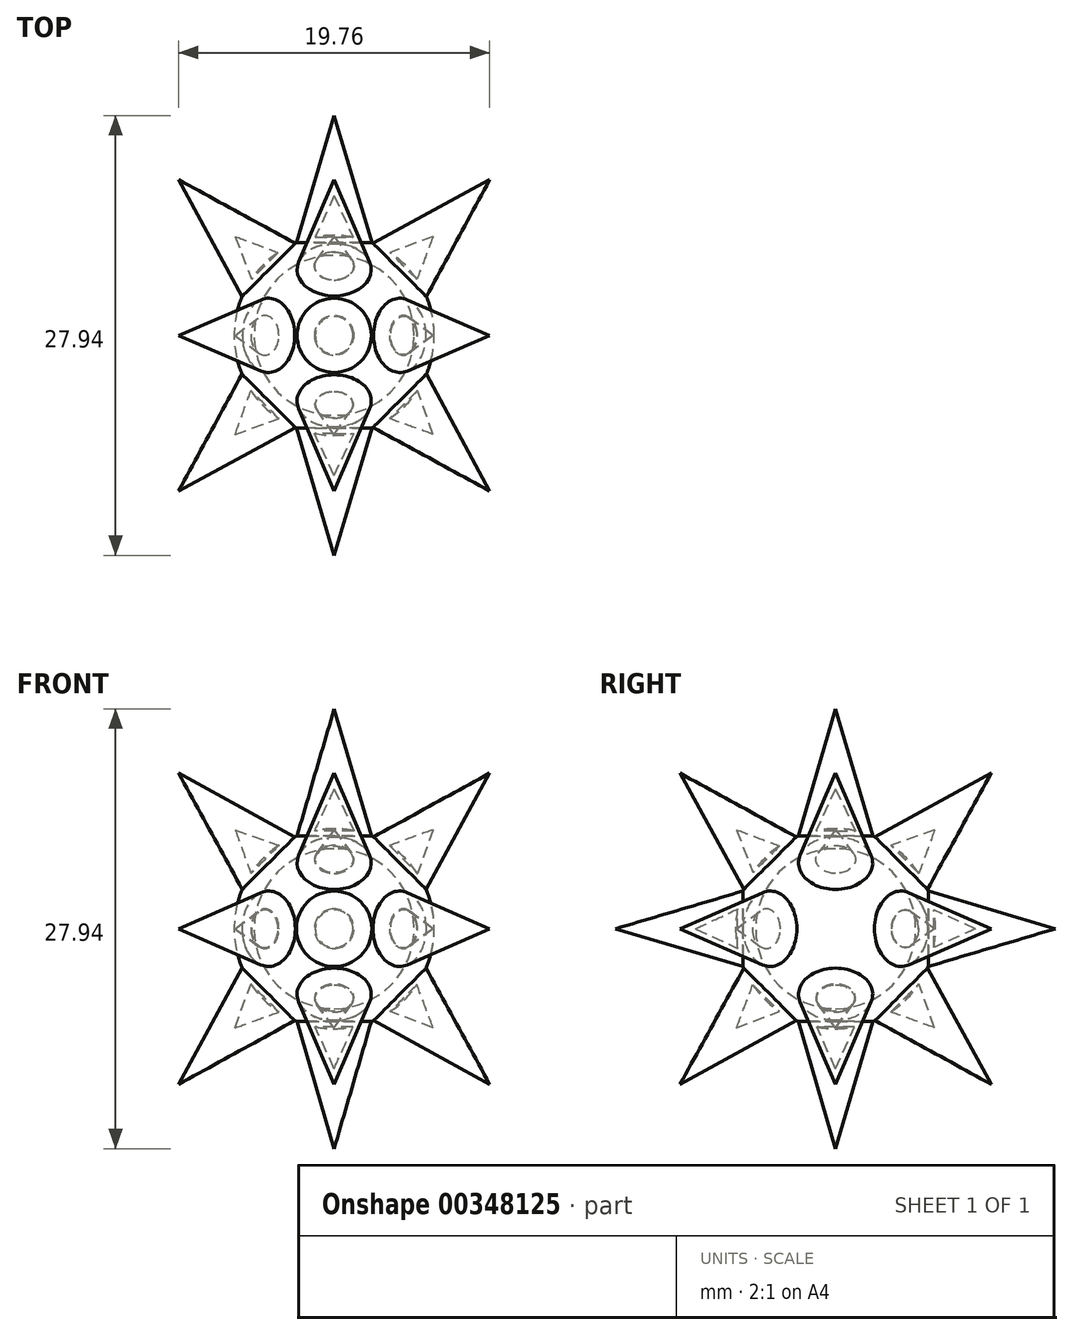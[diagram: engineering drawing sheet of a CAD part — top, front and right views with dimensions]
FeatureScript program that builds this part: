
annotation { "Feature Type Name" : "Feature", "Feature Type Description" : "" }
export const myFeature = defineFeature(function(context is Context, id is Id, definition is map)
    precondition{}
    {
        {
            var Q0;
            Q0=qCreatedBy(makeId("Front.planeOp"),FACE);
            var sketch = newSketch(context, id + "F0", { "sketchPlane" : qUnion([Q0])});
            skCircle(sketch, "E0", {"center": v(0, 0) * mm, "radius": 6.35 * mm});
            skCircle(sketch, "E1", {"center": v(0, 0) * mm, "radius": 5.08 * mm});
            skLineSegment(sketch, "E2", {"start": v(-2.36, 5.9) * mm, "end": v(0, 13.97) * mm});
            skLineSegment(sketch, "E3", {"start": v(0, 13.97) * mm, "end": v(2.36, 5.9) * mm});
            skLineSegment(sketch, "E4", {"start": v(0, 6.89) * mm, "end": v(0, -7.26) * mm, "construction": true});
            skLineSegment(sketch, "E5", {"start": v(0, 13.97) * mm, "end": v(0, -6.35) * mm});
            skLineSegment(sketch, "E6", {"start": v(1.26, 6.22) * mm, "end": v(0, 8.9) * mm});
            skLineSegment(sketch, "E7", {"start": v(0, 8.9) * mm, "end": v(-1.2, 6.24) * mm});
            skLineSegment(sketch, "E8.1.0", {"start": v(-9.88, 9.88) * mm, "end": v(-2.5, 5.84) * mm});
            skLineSegment(sketch, "E8.1.1", {"start": v(-3.51, 5.29) * mm, "end": v(-6.29, 6.29) * mm});
            skLineSegment(sketch, "E8.1.2", {"start": v(-6.29, 6.29) * mm, "end": v(-5.26, 3.56) * mm});
            skLineSegment(sketch, "E8.1.3", {"start": v(-5.84, 2.5) * mm, "end": v(-9.88, 9.88) * mm});
            skLineSegment(sketch, "E8.1.4", {"start": v(-9.88, 9.88) * mm, "end": v(4.5, -4.5) * mm});
            skLineSegment(sketch, "E8.2.0", {"start": v(-13.97, 0) * mm, "end": v(-5.9, 2.36) * mm});
            skLineSegment(sketch, "E8.2.1", {"start": v(-6.22, 1.26) * mm, "end": v(-8.9, 0) * mm});
            skLineSegment(sketch, "E8.2.2", {"start": v(-8.9, 0) * mm, "end": v(-6.24, -1.2) * mm});
            skLineSegment(sketch, "E8.2.3", {"start": v(-5.9, -2.36) * mm, "end": v(-13.97, 0) * mm});
            skLineSegment(sketch, "E8.2.4", {"start": v(-13.97, 0) * mm, "end": v(6.35, 0) * mm});
            skLineSegment(sketch, "E8.3.0", {"start": v(-9.88, -9.88) * mm, "end": v(-5.84, -2.5) * mm});
            skLineSegment(sketch, "E8.3.1", {"start": v(-5.29, -3.51) * mm, "end": v(-6.29, -6.29) * mm});
            skLineSegment(sketch, "E8.3.2", {"start": v(-6.29, -6.29) * mm, "end": v(-3.56, -5.26) * mm});
            skLineSegment(sketch, "E8.3.3", {"start": v(-2.5, -5.84) * mm, "end": v(-9.88, -9.88) * mm});
            skLineSegment(sketch, "E8.3.4", {"start": v(-9.88, -9.88) * mm, "end": v(4.5, 4.5) * mm});
            skLineSegment(sketch, "E8.4.0", {"start": v(0, -13.97) * mm, "end": v(-2.36, -5.9) * mm});
            skLineSegment(sketch, "E8.4.1", {"start": v(-1.26, -6.22) * mm, "end": v(0, -8.9) * mm});
            skLineSegment(sketch, "E8.4.2", {"start": v(0, -8.9) * mm, "end": v(1.2, -6.24) * mm});
            skLineSegment(sketch, "E8.4.3", {"start": v(2.36, -5.9) * mm, "end": v(0, -13.97) * mm});
            skLineSegment(sketch, "E8.4.4", {"start": v(0, -13.97) * mm, "end": v(0, 6.35) * mm});
            skLineSegment(sketch, "E8.5.0", {"start": v(9.88, -9.88) * mm, "end": v(2.5, -5.84) * mm});
            skLineSegment(sketch, "E8.5.1", {"start": v(3.51, -5.29) * mm, "end": v(6.29, -6.29) * mm});
            skLineSegment(sketch, "E8.5.2", {"start": v(6.29, -6.29) * mm, "end": v(5.26, -3.56) * mm});
            skLineSegment(sketch, "E8.5.3", {"start": v(5.84, -2.5) * mm, "end": v(9.88, -9.88) * mm});
            skLineSegment(sketch, "E8.5.4", {"start": v(9.88, -9.88) * mm, "end": v(-4.5, 4.5) * mm});
            skLineSegment(sketch, "E8.6.0", {"start": v(13.97, 0) * mm, "end": v(5.9, -2.36) * mm});
            skLineSegment(sketch, "E8.6.1", {"start": v(6.22, -1.26) * mm, "end": v(8.9, 0) * mm});
            skLineSegment(sketch, "E8.6.2", {"start": v(8.9, 0) * mm, "end": v(6.24, 1.2) * mm});
            skLineSegment(sketch, "E8.6.3", {"start": v(5.9, 2.36) * mm, "end": v(13.97, 0) * mm});
            skLineSegment(sketch, "E8.6.4", {"start": v(13.97, 0) * mm, "end": v(-6.35, 0) * mm});
            skLineSegment(sketch, "E8.7.0", {"start": v(9.88, 9.88) * mm, "end": v(5.84, 2.5) * mm});
            skLineSegment(sketch, "E8.7.1", {"start": v(5.29, 3.51) * mm, "end": v(6.29, 6.29) * mm});
            skLineSegment(sketch, "E8.7.2", {"start": v(6.29, 6.29) * mm, "end": v(3.56, 5.26) * mm});
            skLineSegment(sketch, "E8.7.3", {"start": v(2.5, 5.84) * mm, "end": v(9.88, 9.88) * mm});
            skLineSegment(sketch, "E8.7.4", {"start": v(9.88, 9.88) * mm, "end": v(-4.5, -4.5) * mm});
            skSolve(sketch);
        }
        {
            var Q0;
            {var subQ1=sQuery(id+"F0.wireOp",EDGE,"E0");var subQ5=makeQuery(id+"F0.imprint","INTERSECT",VERTEX,{"derivedFrom":[subQ1,sQuery(id+"F0.wireOp",EDGE,"E3")]});Q0=makeQuery(id+"F0.imprint","IMPRINT",FACE,{"disambiguationData":[TD([[makeQuery(id+"F0.imprint","IMPRINT",EDGE,{"disambiguationData":[TD([[subQ5,-1.0]])],"derivedFrom":subQ1}),1.0]])]});}
            var Q1;
            {var subQ0=sQuery(id+"F0.wireOp",EDGE,"E0");var subQ4=makeQuery(id+"F0.imprint","INTERSECT",VERTEX,{"derivedFrom":[subQ0,sQuery(id+"F0.wireOp",EDGE,"E8.6.2")]});Q1=makeQuery(id+"F0.imprint","IMPRINT",FACE,{"disambiguationData":[TD([[makeQuery(id+"F0.imprint","IMPRINT",EDGE,{"disambiguationData":[TD([[subQ4,1.0]])],"derivedFrom":subQ0}),1.0]])]});}
            var Q2;
            {var subQ0=sQuery(id+"F0.wireOp",EDGE,"E0");var subQ4=makeQuery(id+"F0.imprint","INTERSECT",VERTEX,{"derivedFrom":[subQ0,sQuery(id+"F0.wireOp",EDGE,"E8.5.2")]});Q2=makeQuery(id+"F0.imprint","IMPRINT",FACE,{"disambiguationData":[TD([[makeQuery(id+"F0.imprint","IMPRINT",EDGE,{"disambiguationData":[TD([[subQ4,1.0]])],"derivedFrom":subQ0}),1.0]])]});}
            var Q3;
            {var subQ0=sQuery(id+"F0.wireOp",EDGE,"E0");var subQ8=makeQuery(id+"F0.imprint","INTERSECT",VERTEX,{"derivedFrom":[subQ0,sQuery(id+"F0.wireOp",EDGE,"E8.4.2")]});Q3=makeQuery(id+"F0.imprint","IMPRINT",FACE,{"disambiguationData":[TD([[makeQuery(id+"F0.imprint","IMPRINT",EDGE,{"disambiguationData":[TD([[subQ8,1.0]])],"derivedFrom":subQ0}),1.0]])]});}
            var Q4;
            Q4=sQuery(id+"F0.wireOp",EDGE,"E4");
            revolve(context, id + "F1", {"entities" : qUnion([Q0, Q1, Q2, Q3]), "axis" : qUnion([Q4]), "revolveType" : RevolveType.FULL});
        }
        {
            var Q0;
            {var subQ0=sQuery(id+"F0.wireOp",EDGE,"E3");Q0=makeQuery(id+"F0.imprint","IMPRINT",FACE,{"disambiguationData":[TD([[makeQuery(id+"F0.imprint","IMPRINT",EDGE,{"derivedFrom":subQ0}),-1.0]])]});}
            var Q1;
            {var subQ0=sQuery(id+"F0.wireOp",EDGE,"E8.4.2");Q1=makeQuery(id+"F0.imprint","IMPRINT",FACE,{"disambiguationData":[TD([[makeQuery(id+"F0.imprint","IMPRINT",EDGE,{"derivedFrom":subQ0}),-1.0]])]});}
            var Q2;
            Q2=sQuery(id+"F0.wireOp",EDGE,"E5");
            revolve(context, id + "F2", {"operationType" : NewBodyOperationType.ADD, "entities" : qUnion([Q0, Q1]), "axis" : qUnion([Q2]), "revolveType" : RevolveType.FULL});
        }
        {
            var Q0;
            {var subQ0=sQuery(id+"F0.wireOp",EDGE,"E8.5.2");Q0=makeQuery(id+"F0.imprint","IMPRINT",FACE,{"disambiguationData":[TD([[makeQuery(id+"F0.imprint","IMPRINT",EDGE,{"derivedFrom":subQ0}),-1.0]])]});}
            var Q1;
            {var subQ0=sQuery(id+"F0.wireOp",EDGE,"E8.1.0");Q1=makeQuery(id+"F0.imprint","IMPRINT",FACE,{"disambiguationData":[TD([[makeQuery(id+"F0.imprint","IMPRINT",EDGE,{"derivedFrom":subQ0}),-1.0]])]});}
            var Q2;
            Q2=sQuery(id+"F0.wireOp",EDGE,"E8.1.4");
            revolve(context, id + "F3", {"operationType" : NewBodyOperationType.ADD, "entities" : qUnion([Q0, Q1]), "axis" : qUnion([Q2]), "revolveType" : RevolveType.FULL});
        }
        {
            var Q0;
            {var subQ0=sQuery(id+"F0.wireOp",EDGE,"E8.7.0");Q0=makeQuery(id+"F0.imprint","IMPRINT",FACE,{"disambiguationData":[TD([[makeQuery(id+"F0.imprint","IMPRINT",EDGE,{"derivedFrom":subQ0}),-1.0]])]});}
            var Q1;
            {var subQ0=sQuery(id+"F0.wireOp",EDGE,"E8.3.0");Q1=makeQuery(id+"F0.imprint","IMPRINT",FACE,{"disambiguationData":[TD([[makeQuery(id+"F0.imprint","IMPRINT",EDGE,{"derivedFrom":subQ0}),-1.0]])]});}
            var Q2;
            Q2=sQuery(id+"F0.wireOp",EDGE,"E8.7.4");
            revolve(context, id + "F4", {"operationType" : NewBodyOperationType.ADD, "entities" : qUnion([Q0, Q1]), "axis" : qUnion([Q2]), "revolveType" : RevolveType.FULL});
        }
        {
            var Q0;
            Q0=qCreatedBy(makeId("Top.planeOp"),FACE);
            var sketch = newSketch(context, id + "F5", { "sketchPlane" : qUnion([Q0])});
            skCircle(sketch, "E9", {"center": v(0, 0) * mm, "radius": 6.35 * mm});
            skCircle(sketch, "E10", {"center": v(0, 0) * mm, "radius": 5.08 * mm});
            skLineSegment(sketch, "E11.1.0", {"start": v(-9.88, 9.88) * mm, "end": v(-2.46, 5.85) * mm});
            skLineSegment(sketch, "E11.1.1", {"start": v(-3.51, 5.29) * mm, "end": v(-6.29, 6.29) * mm});
            skLineSegment(sketch, "E11.1.2", {"start": v(-6.29, 6.29) * mm, "end": v(-5.26, 3.56) * mm});
            skLineSegment(sketch, "E11.1.3", {"start": v(-5.85, 2.46) * mm, "end": v(-9.88, 9.88) * mm});
            skLineSegment(sketch, "E11.1.4", {"start": v(-9.88, 9.88) * mm, "end": v(4.5, -4.5) * mm});
            skLineSegment(sketch, "E12.1.0", {"start": v(-13.97, 0) * mm, "end": v(-5.88, 2.4) * mm});
            skLineSegment(sketch, "E12.1.1", {"start": v(-6.22, 1.26) * mm, "end": v(-8.89, 0) * mm});
            skLineSegment(sketch, "E12.1.2", {"start": v(-13.97, 0) * mm, "end": v(6.35, 0) * mm});
            skLineSegment(sketch, "E12.1.3", {"start": v(-8.89, 0) * mm, "end": v(-6.24, -1.2) * mm});
            skLineSegment(sketch, "E12.1.4", {"start": v(-5.88, -2.4) * mm, "end": v(-13.97, 0) * mm});
            skLineSegment(sketch, "E12.2.0", {"start": v(-9.88, -9.88) * mm, "end": v(-5.85, -2.46) * mm});
            skLineSegment(sketch, "E12.2.1", {"start": v(-5.29, -3.51) * mm, "end": v(-6.29, -6.29) * mm});
            skLineSegment(sketch, "E12.2.2", {"start": v(-9.88, -9.88) * mm, "end": v(4.5, 4.5) * mm});
            skLineSegment(sketch, "E12.2.3", {"start": v(-6.29, -6.29) * mm, "end": v(-3.56, -5.26) * mm});
            skLineSegment(sketch, "E12.2.4", {"start": v(-2.46, -5.85) * mm, "end": v(-9.88, -9.88) * mm});
            skLineSegment(sketch, "E12.3.0", {"start": v(0, -13.97) * mm, "end": v(-2.4, -5.88) * mm});
            skLineSegment(sketch, "E12.3.1", {"start": v(-1.26, -6.22) * mm, "end": v(0, -8.89) * mm});
            skLineSegment(sketch, "E12.3.2", {"start": v(0, -13.97) * mm, "end": v(0, 6.35) * mm});
            skLineSegment(sketch, "E12.3.3", {"start": v(0, -8.89) * mm, "end": v(1.2, -6.24) * mm});
            skLineSegment(sketch, "E12.3.4", {"start": v(2.4, -5.88) * mm, "end": v(0, -13.97) * mm});
            skLineSegment(sketch, "E12.4.0", {"start": v(9.88, -9.88) * mm, "end": v(2.46, -5.85) * mm});
            skLineSegment(sketch, "E12.4.1", {"start": v(3.51, -5.29) * mm, "end": v(6.29, -6.29) * mm});
            skLineSegment(sketch, "E12.4.2", {"start": v(9.88, -9.88) * mm, "end": v(-4.5, 4.5) * mm});
            skLineSegment(sketch, "E12.4.3", {"start": v(6.29, -6.29) * mm, "end": v(5.26, -3.56) * mm});
            skLineSegment(sketch, "E12.4.4", {"start": v(5.85, -2.46) * mm, "end": v(9.88, -9.88) * mm});
            skLineSegment(sketch, "E12.5.0", {"start": v(13.97, 0) * mm, "end": v(5.88, -2.4) * mm});
            skLineSegment(sketch, "E12.5.1", {"start": v(6.22, -1.26) * mm, "end": v(8.89, 0) * mm});
            skLineSegment(sketch, "E12.5.2", {"start": v(13.97, 0) * mm, "end": v(-6.35, 0) * mm});
            skLineSegment(sketch, "E12.5.3", {"start": v(8.89, 0) * mm, "end": v(6.24, 1.2) * mm});
            skLineSegment(sketch, "E12.5.4", {"start": v(5.88, 2.4) * mm, "end": v(13.97, 0) * mm});
            skLineSegment(sketch, "E12.6.0", {"start": v(9.88, 9.88) * mm, "end": v(5.85, 2.46) * mm});
            skLineSegment(sketch, "E12.6.1", {"start": v(5.29, 3.51) * mm, "end": v(6.29, 6.29) * mm});
            skLineSegment(sketch, "E12.6.2", {"start": v(9.88, 9.88) * mm, "end": v(-4.5, -4.5) * mm});
            skLineSegment(sketch, "E12.6.3", {"start": v(6.29, 6.29) * mm, "end": v(3.56, 5.26) * mm});
            skLineSegment(sketch, "E12.6.4", {"start": v(2.46, 5.85) * mm, "end": v(9.88, 9.88) * mm});
            skLineSegment(sketch, "E12.7.0", {"start": v(0, 13.97) * mm, "end": v(2.4, 5.88) * mm});
            skLineSegment(sketch, "E12.7.1", {"start": v(1.26, 6.22) * mm, "end": v(0, 8.89) * mm});
            skLineSegment(sketch, "E12.7.2", {"start": v(0, 13.97) * mm, "end": v(0, -6.35) * mm});
            skLineSegment(sketch, "E12.7.3", {"start": v(0, 8.89) * mm, "end": v(-1.2, 6.24) * mm});
            skLineSegment(sketch, "E12.7.4", {"start": v(-2.4, 5.88) * mm, "end": v(0, 13.97) * mm});
            skSolve(sketch);
        }
        {
            var Q0;
            {var subQ0=sQuery(id+"F5.wireOp",EDGE,"E12.2.0");Q0=makeQuery(id+"F5.imprint","IMPRINT",FACE,{"disambiguationData":[TD([[makeQuery(id+"F5.imprint","IMPRINT",EDGE,{"derivedFrom":subQ0}),-1.0]])]});}
            var Q1;
            {var subQ0=sQuery(id+"F5.wireOp",EDGE,"E12.6.3");Q1=makeQuery(id+"F5.imprint","IMPRINT",FACE,{"disambiguationData":[TD([[makeQuery(id+"F5.imprint","IMPRINT",EDGE,{"derivedFrom":subQ0}),-1.0]])]});}
            var Q2;
            Q2=sQuery(id+"F5.wireOp",EDGE,"E12.2.2");
            revolve(context, id + "F6", {"operationType" : NewBodyOperationType.ADD, "entities" : qUnion([Q0, Q1]), "axis" : qUnion([Q2]), "revolveType" : RevolveType.FULL});
        }
        {
            var Q0;
            {var subQ0=sQuery(id+"F5.wireOp",EDGE,"E12.3.0");Q0=makeQuery(id+"F5.imprint","IMPRINT",FACE,{"disambiguationData":[TD([[makeQuery(id+"F5.imprint","IMPRINT",EDGE,{"derivedFrom":subQ0}),-1.0]])]});}
            var Q1;
            {var subQ0=sQuery(id+"F5.wireOp",EDGE,"E12.7.3");Q1=makeQuery(id+"F5.imprint","IMPRINT",FACE,{"disambiguationData":[TD([[makeQuery(id+"F5.imprint","IMPRINT",EDGE,{"derivedFrom":subQ0}),-1.0]])]});}
            var Q2;
            Q2=sQuery(id+"F5.wireOp",EDGE,"E12.3.2");
            revolve(context, id + "F7", {"operationType" : NewBodyOperationType.ADD, "entities" : qUnion([Q0, Q1]), "axis" : qUnion([Q2]), "revolveType" : RevolveType.FULL});
        }
        {
            var Q0;
            {var subQ0=sQuery(id+"F5.wireOp",EDGE,"E12.4.0");Q0=makeQuery(id+"F5.imprint","IMPRINT",FACE,{"disambiguationData":[TD([[makeQuery(id+"F5.imprint","IMPRINT",EDGE,{"derivedFrom":subQ0}),-1.0]])]});}
            var Q1;
            {var subQ0=sQuery(id+"F5.wireOp",EDGE,"E11.1.2");Q1=makeQuery(id+"F5.imprint","IMPRINT",FACE,{"disambiguationData":[TD([[makeQuery(id+"F5.imprint","IMPRINT",EDGE,{"derivedFrom":subQ0}),-1.0]])]});}
            var Q2;
            Q2=sQuery(id+"F5.wireOp",EDGE,"E12.4.2");
            revolve(context, id + "F8", {"operationType" : NewBodyOperationType.ADD, "entities" : qUnion([Q0, Q1]), "axis" : qUnion([Q2]), "revolveType" : RevolveType.FULL});
        }
        {
            var Q0;
            Q0=qCreatedBy(makeId("Right.planeOp"),FACE);
            var sketch = newSketch(context, id + "F9", { "sketchPlane" : qUnion([Q0])});
            skCircle(sketch, "E13", {"center": v(0, 0) * mm, "radius": 6.35 * mm});
            skCircle(sketch, "E14", {"center": v(0, 0) * mm, "radius": 5.08 * mm});
            skLineSegment(sketch, "E15", {"start": v(-2.36, 5.9) * mm, "end": v(0, 13.97) * mm});
            skLineSegment(sketch, "E16", {"start": v(0, 13.97) * mm, "end": v(2.36, 5.9) * mm});
            skLineSegment(sketch, "E17", {"start": v(0, 13.97) * mm, "end": v(0, -6.35) * mm});
            skLineSegment(sketch, "E18", {"start": v(1.26, 6.22) * mm, "end": v(0, 8.9) * mm});
            skLineSegment(sketch, "E19", {"start": v(0, 8.89) * mm, "end": v(-1.2, 6.24) * mm});
            skLineSegment(sketch, "E20.1.0", {"start": v(-9.88, 9.88) * mm, "end": v(-2.5, 5.84) * mm});
            skLineSegment(sketch, "E20.1.1", {"start": v(-5.84, 2.5) * mm, "end": v(-9.88, 9.88) * mm});
            skLineSegment(sketch, "E20.1.2", {"start": v(-9.88, 9.88) * mm, "end": v(4.5, -4.5) * mm});
            skLineSegment(sketch, "E20.1.3", {"start": v(-3.51, 5.29) * mm, "end": v(-6.29, 6.29) * mm});
            skLineSegment(sketch, "E20.1.4", {"start": v(-6.29, 6.29) * mm, "end": v(-5.26, 3.56) * mm});
            skLineSegment(sketch, "E20.2.0", {"start": v(-13.97, 0) * mm, "end": v(-5.9, 2.36) * mm});
            skLineSegment(sketch, "E20.2.1", {"start": v(-5.9, -2.36) * mm, "end": v(-13.97, 0) * mm});
            skLineSegment(sketch, "E20.2.2", {"start": v(-13.97, 0) * mm, "end": v(6.35, 0) * mm});
            skLineSegment(sketch, "E20.2.3", {"start": v(-6.22, 1.26) * mm, "end": v(-8.9, 0) * mm});
            skLineSegment(sketch, "E20.2.4", {"start": v(-8.89, 0) * mm, "end": v(-6.24, -1.2) * mm});
            skLineSegment(sketch, "E20.3.0", {"start": v(-9.88, -9.88) * mm, "end": v(-5.84, -2.5) * mm});
            skLineSegment(sketch, "E20.3.1", {"start": v(-2.5, -5.84) * mm, "end": v(-9.88, -9.88) * mm});
            skLineSegment(sketch, "E20.3.2", {"start": v(-9.88, -9.88) * mm, "end": v(4.5, 4.5) * mm});
            skLineSegment(sketch, "E20.3.3", {"start": v(-5.29, -3.51) * mm, "end": v(-6.29, -6.29) * mm});
            skLineSegment(sketch, "E20.3.4", {"start": v(-6.29, -6.29) * mm, "end": v(-3.56, -5.26) * mm});
            skLineSegment(sketch, "E20.4.0", {"start": v(0, -13.97) * mm, "end": v(-2.36, -5.9) * mm});
            skLineSegment(sketch, "E20.4.1", {"start": v(2.36, -5.9) * mm, "end": v(0, -13.97) * mm});
            skLineSegment(sketch, "E20.4.2", {"start": v(0, -13.97) * mm, "end": v(0, 6.35) * mm});
            skLineSegment(sketch, "E20.4.3", {"start": v(-1.26, -6.22) * mm, "end": v(0, -8.9) * mm});
            skLineSegment(sketch, "E20.4.4", {"start": v(0, -8.89) * mm, "end": v(1.2, -6.24) * mm});
            skLineSegment(sketch, "E20.5.0", {"start": v(9.88, -9.88) * mm, "end": v(2.5, -5.84) * mm});
            skLineSegment(sketch, "E20.5.1", {"start": v(5.84, -2.5) * mm, "end": v(9.88, -9.88) * mm});
            skLineSegment(sketch, "E20.5.2", {"start": v(9.88, -9.88) * mm, "end": v(-4.5, 4.5) * mm});
            skLineSegment(sketch, "E20.5.3", {"start": v(3.51, -5.29) * mm, "end": v(6.29, -6.29) * mm});
            skLineSegment(sketch, "E20.5.4", {"start": v(6.29, -6.29) * mm, "end": v(5.26, -3.56) * mm});
            skLineSegment(sketch, "E20.6.0", {"start": v(13.97, 0) * mm, "end": v(5.9, -2.36) * mm});
            skLineSegment(sketch, "E20.6.1", {"start": v(5.9, 2.36) * mm, "end": v(13.97, 0) * mm});
            skLineSegment(sketch, "E20.6.2", {"start": v(13.97, 0) * mm, "end": v(-6.35, 0) * mm});
            skLineSegment(sketch, "E20.6.3", {"start": v(6.22, -1.26) * mm, "end": v(8.9, 0) * mm});
            skLineSegment(sketch, "E20.6.4", {"start": v(8.89, 0) * mm, "end": v(6.24, 1.2) * mm});
            skLineSegment(sketch, "E20.7.0", {"start": v(9.88, 9.88) * mm, "end": v(5.84, 2.5) * mm});
            skLineSegment(sketch, "E20.7.1", {"start": v(2.5, 5.84) * mm, "end": v(9.88, 9.88) * mm});
            skLineSegment(sketch, "E20.7.2", {"start": v(9.88, 9.88) * mm, "end": v(-4.5, -4.5) * mm});
            skLineSegment(sketch, "E20.7.3", {"start": v(5.29, 3.51) * mm, "end": v(6.29, 6.29) * mm});
            skLineSegment(sketch, "E20.7.4", {"start": v(6.29, 6.29) * mm, "end": v(3.56, 5.26) * mm});
            skSolve(sketch);
        }
        {
            var Q0;
            {var subQ0=sQuery(id+"F9.wireOp",EDGE,"E20.1.1");Q0=makeQuery(id+"F9.imprint","IMPRINT",FACE,{"disambiguationData":[TD([[makeQuery(id+"F9.imprint","IMPRINT",EDGE,{"derivedFrom":subQ0}),-1.0]])]});}
            var Q1;
            {var subQ0=sQuery(id+"F9.wireOp",EDGE,"E20.5.0");Q1=makeQuery(id+"F9.imprint","IMPRINT",FACE,{"disambiguationData":[TD([[makeQuery(id+"F9.imprint","IMPRINT",EDGE,{"derivedFrom":subQ0}),-1.0]])]});}
            var Q2;
            Q2=sQuery(id+"F9.wireOp",EDGE,"E20.1.2");
            revolve(context, id + "F10", {"operationType" : NewBodyOperationType.ADD, "entities" : qUnion([Q0, Q1]), "axis" : qUnion([Q2]), "revolveType" : RevolveType.FULL});
        }
        {
            var Q0;
            {var subQ0=sQuery(id+"F9.wireOp",EDGE,"E20.3.1");Q0=makeQuery(id+"F9.imprint","IMPRINT",FACE,{"disambiguationData":[TD([[makeQuery(id+"F9.imprint","IMPRINT",EDGE,{"derivedFrom":subQ0}),-1.0]])]});}
            var Q1;
            {var subQ0=sQuery(id+"F9.wireOp",EDGE,"E20.7.0");Q1=makeQuery(id+"F9.imprint","IMPRINT",FACE,{"disambiguationData":[TD([[makeQuery(id+"F9.imprint","IMPRINT",EDGE,{"derivedFrom":subQ0}),-1.0]])]});}
            var Q2;
            Q2=sQuery(id+"F9.wireOp",EDGE,"E20.3.2");
            revolve(context, id + "F11", {"operationType" : NewBodyOperationType.ADD, "entities" : qUnion([Q0, Q1]), "axis" : qUnion([Q2]), "revolveType" : RevolveType.FULL});
        }
    });
